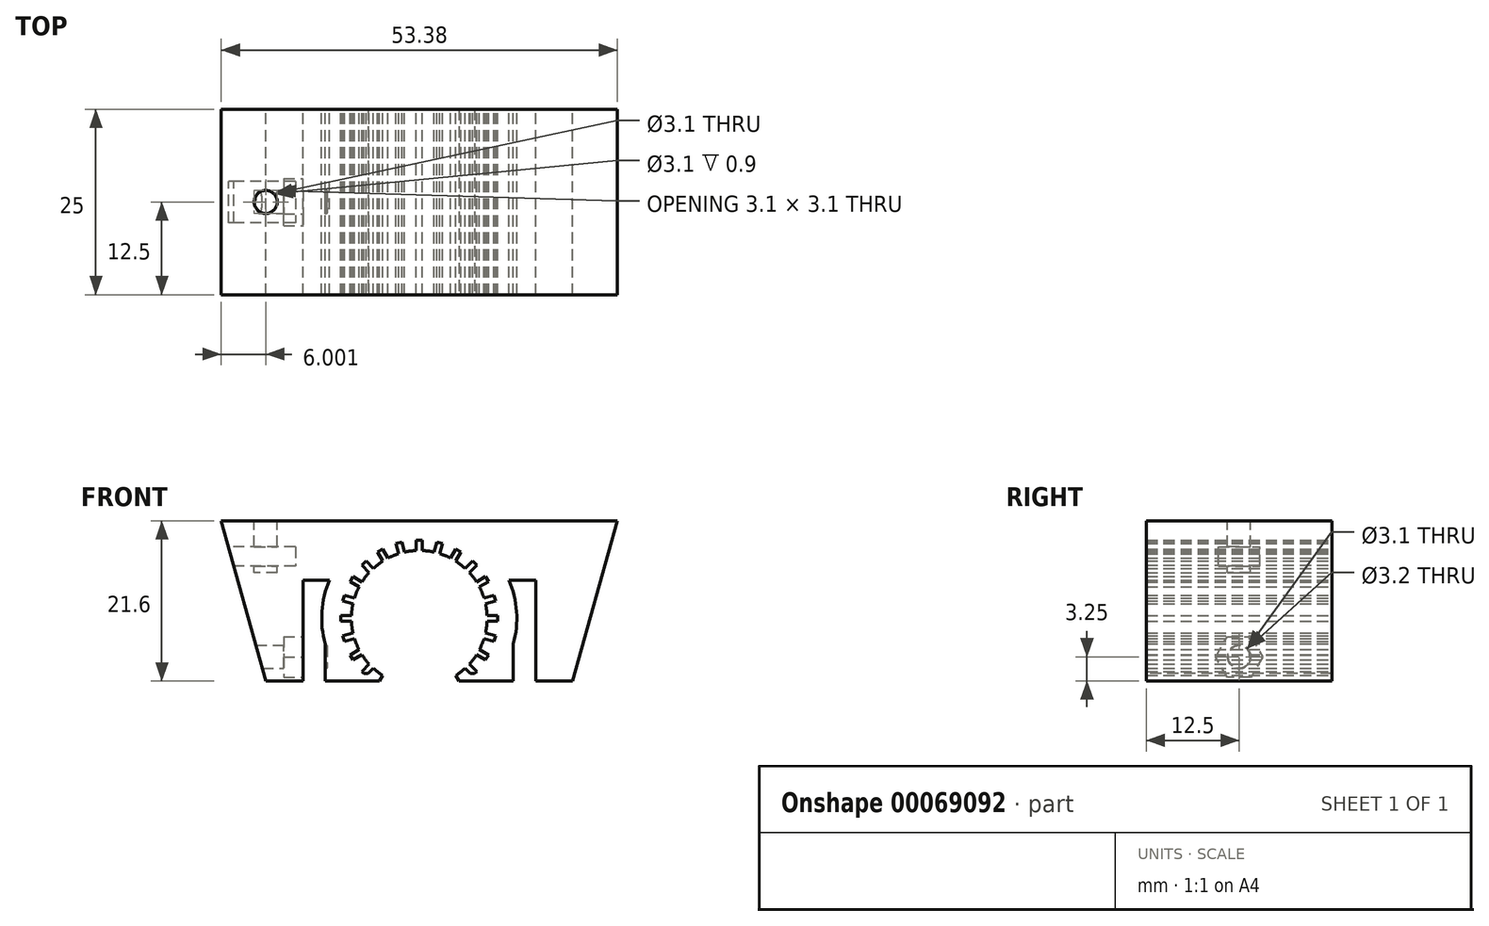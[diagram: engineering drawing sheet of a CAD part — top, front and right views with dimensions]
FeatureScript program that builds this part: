
annotation { "Feature Type Name" : "Feature", "Feature Type Description" : "" }
export const myFeature = defineFeature(function(context is Context, id is Id, definition is map)
    precondition{}
    {
        {
            var Q0;
            Q0=qCreatedBy(makeId("Front.planeOp"),FACE);
            var sketch = newSketch(context, id + "F0", { "sketchPlane" : qUnion([Q0])});
            skCircle(sketch, "E0", {"center": v(0, 0) * mm, "radius": 8.95 * mm, "construction": true});
            skLineSegment(sketch, "E1", {"start": v(-47.47, -8.95) * mm, "end": v(47.47, -8.95) * mm, "construction": true});
            skPoint(sketch, "E2", {"position": v(0, -8.95) * mm});
            skLineSegment(sketch, "E3", {"start": v(0, 13.15) * mm, "end": v(26.69, 13.15) * mm});
            skLineSegment(sketch, "E4", {"start": v(26.69, 13.15) * mm, "end": v(20.69, -8.45) * mm});
            skLineSegment(sketch, "E5", {"start": v(20.69, -8.45) * mm, "end": v(15.69, -8.45) * mm});
            skLineSegment(sketch, "E6", {"start": v(15.69, -8.45) * mm, "end": v(15.69, 5.15) * mm});
            skLineSegment(sketch, "E7", {"start": v(15.69, 5.15) * mm, "end": v(12.1, 5.15) * mm});
            skArc(sketch, "E8", {"start": v(3.5, -8.45) * mm, "mid": v(8.97, 1.79) * mm, "end": v(0, 9.15) * mm});
            skLineSegment(sketch, "E9", {"start": v(3.5, -8.45) * mm, "end": v(12.69, -8.45) * mm});
            skArc(sketch, "E10", {"start": v(12.69, -3.45) * mm, "mid": v(13.12, 0.9) * mm, "end": v(12.1, 5.15) * mm});
            skLineSegment(sketch, "E11", {"start": v(12.69, -3.45) * mm, "end": v(12.69, -8.45) * mm});
            skLineSegment(sketch, "E12", {"start": v(0, 0) * mm, "end": v(0, -8.95) * mm, "construction": true});
            skArc(sketch, "E13.MirrorCS", {"start": v(-12.69, -3.45) * mm, "mid": v(-13.12, 0.9) * mm, "end": v(-12.1, 5.15) * mm});
            skLineSegment(sketch, "E14.MirrorCS", {"start": v(0, 13.15) * mm, "end": v(-26.69, 13.15) * mm});
            skLineSegment(sketch, "E15.MirrorCS", {"start": v(-12.69, -3.45) * mm, "end": v(-12.69, -8.45) * mm});
            skLineSegment(sketch, "E16.MirrorCS", {"start": v(-3.5, -8.45) * mm, "end": v(-12.69, -8.45) * mm});
            skLineSegment(sketch, "E17.MirrorCS", {"start": v(-26.69, 13.15) * mm, "end": v(-20.69, -8.45) * mm});
            skLineSegment(sketch, "E18.MirrorCS", {"start": v(-15.69, -8.45) * mm, "end": v(-15.69, 5.15) * mm});
            skArc(sketch, "E19.MirrorCS", {"start": v(-3.5, -8.45) * mm, "mid": v(-8.97, 1.79) * mm, "end": v(0, 9.15) * mm});
            skLineSegment(sketch, "E20.MirrorCS", {"start": v(-15.69, 5.15) * mm, "end": v(-12.1, 5.15) * mm});
            skLineSegment(sketch, "E21.MirrorCS", {"start": v(-20.69, -8.45) * mm, "end": v(-15.69, -8.45) * mm});
            skSolve(sketch);
        }
        {
            var Q0;
            Q0=makeQuery(id+"F0.imprint","IMPRINT",FACE,{"disambiguationData":[TD([[makeQuery(id+"F0.imprint","IMPRINT",EDGE,{"derivedFrom":sQuery(id+"F0.wireOp",EDGE,"E3")}),-1.0]])]});
            extrude(context, id + "F1", {"entities" : qUnion([Q0]), "depth" : 25 * mm, "offsetDistance" : 25 * mm});
        }
        {
            var Q0;
            Q0=makeQuery(id+"F1.opExtrude","CAP_FACE",FACE,{"disambiguationData":[OSD([sQuery(id+"F0.wireOp",EDGE,"E3"),sQuery(id+"F0.wireOp",EDGE,"E4"),sQuery(id+"F0.wireOp",EDGE,"E5"),sQuery(id+"F0.wireOp",EDGE,"E6"),sQuery(id+"F0.wireOp",EDGE,"E7"),sQuery(id+"F0.wireOp",EDGE,"E8"),sQuery(id+"F0.wireOp",EDGE,"E9"),sQuery(id+"F0.wireOp",EDGE,"E10"),sQuery(id+"F0.wireOp",EDGE,"E11"),sQuery(id+"F0.wireOp",EDGE,"E13.MirrorCS"),sQuery(id+"F0.wireOp",EDGE,"E14.MirrorCS"),sQuery(id+"F0.wireOp",EDGE,"E15.MirrorCS"),sQuery(id+"F0.wireOp",EDGE,"E16.MirrorCS"),sQuery(id+"F0.wireOp",EDGE,"E17.MirrorCS"),sQuery(id+"F0.wireOp",EDGE,"E18.MirrorCS"),sQuery(id+"F0.wireOp",EDGE,"E19.MirrorCS"),sQuery(id+"F0.wireOp",EDGE,"E20.MirrorCS"),sQuery(id+"F0.wireOp",EDGE,"E21.MirrorCS")])],"isStart":true});
            var sketch = newSketch(context, id + "F2", { "sketchPlane" : qUnion([Q0])});
            skLineSegment(sketch, "E22.bottom", {"start": v(-10.55, 0.4) * mm, "end": v(-7.35, 0.4) * mm});
            skLineSegment(sketch, "E22.top", {"start": v(-10.55, -0.4) * mm, "end": v(-7.35, -0.4) * mm});
            skLineSegment(sketch, "E22.left", {"start": v(-10.55, 0.4) * mm, "end": v(-10.55, -0.4) * mm});
            skLineSegment(sketch, "E22.right", {"start": v(-7.35, 0.4) * mm, "end": v(-7.35, -0.4) * mm});
            skPoint(sketch, "E22.middle", {"position": v(-8.95, 0) * mm});
            skPoint(sketch, "E23.1.0", {"position": v(-8.65, -2.32) * mm});
            skLineSegment(sketch, "E23.1.1", {"start": v(-10.3, -2.34) * mm, "end": v(-7.2, -1.52) * mm});
            skLineSegment(sketch, "E23.1.2", {"start": v(-7.2, -1.52) * mm, "end": v(-7, -2.29) * mm});
            skLineSegment(sketch, "E23.1.3", {"start": v(-10.09, -3.12) * mm, "end": v(-7, -2.29) * mm});
            skLineSegment(sketch, "E23.1.4", {"start": v(-10.3, -2.34) * mm, "end": v(-10.09, -3.12) * mm});
            skPoint(sketch, "E23.2.0", {"position": v(-7.75, -4.47) * mm});
            skLineSegment(sketch, "E23.2.1", {"start": v(-9.34, -4.93) * mm, "end": v(-6.57, -3.33) * mm});
            skLineSegment(sketch, "E23.2.2", {"start": v(-6.57, -3.33) * mm, "end": v(-6.17, -4.02) * mm});
            skLineSegment(sketch, "E23.2.3", {"start": v(-8.94, -5.62) * mm, "end": v(-6.17, -4.02) * mm});
            skLineSegment(sketch, "E23.2.4", {"start": v(-9.34, -4.93) * mm, "end": v(-8.94, -5.62) * mm});
            skPoint(sketch, "E23.3.0", {"position": v(-6.33, -6.33) * mm});
            skLineSegment(sketch, "E23.3.1", {"start": v(-7.74, -7.18) * mm, "end": v(-5.48, -4.91) * mm});
            skLineSegment(sketch, "E23.3.2", {"start": v(-5.48, -4.91) * mm, "end": v(-4.91, -5.48) * mm});
            skLineSegment(sketch, "E23.3.3", {"start": v(-7.18, -7.74) * mm, "end": v(-4.91, -5.48) * mm});
            skLineSegment(sketch, "E23.3.4", {"start": v(-7.74, -7.18) * mm, "end": v(-7.18, -7.74) * mm});
            skPoint(sketch, "E23.4.0", {"position": v(-4.48, -7.75) * mm});
            skLineSegment(sketch, "E23.4.1", {"start": v(-5.62, -8.94) * mm, "end": v(-4.02, -6.17) * mm});
            skLineSegment(sketch, "E23.4.2", {"start": v(-4.02, -6.17) * mm, "end": v(-3.33, -6.57) * mm});
            skLineSegment(sketch, "E23.4.3", {"start": v(-4.93, -9.34) * mm, "end": v(-3.33, -6.57) * mm});
            skLineSegment(sketch, "E23.4.4", {"start": v(-5.62, -8.94) * mm, "end": v(-4.93, -9.34) * mm});
            skPoint(sketch, "E23.5.0", {"position": v(-2.32, -8.65) * mm});
            skLineSegment(sketch, "E23.5.1", {"start": v(-3.12, -10.09) * mm, "end": v(-2.29, -7) * mm});
            skLineSegment(sketch, "E23.5.2", {"start": v(-2.29, -7) * mm, "end": v(-1.52, -7.2) * mm});
            skLineSegment(sketch, "E23.5.3", {"start": v(-2.34, -10.3) * mm, "end": v(-1.52, -7.2) * mm});
            skLineSegment(sketch, "E23.5.4", {"start": v(-3.12, -10.09) * mm, "end": v(-2.34, -10.3) * mm});
            skPoint(sketch, "E23.6.0", {"position": v(0, -8.95) * mm});
            skLineSegment(sketch, "E23.6.1", {"start": v(-0.4, -10.55) * mm, "end": v(-0.4, -7.35) * mm});
            skLineSegment(sketch, "E23.6.2", {"start": v(-0.4, -7.35) * mm, "end": v(0.4, -7.35) * mm});
            skLineSegment(sketch, "E23.6.3", {"start": v(0.4, -10.55) * mm, "end": v(0.4, -7.35) * mm});
            skLineSegment(sketch, "E23.6.4", {"start": v(-0.4, -10.55) * mm, "end": v(0.4, -10.55) * mm});
            skPoint(sketch, "E23.7.0", {"position": v(2.32, -8.65) * mm});
            skLineSegment(sketch, "E23.7.1", {"start": v(2.34, -10.3) * mm, "end": v(1.52, -7.2) * mm});
            skLineSegment(sketch, "E23.7.2", {"start": v(1.52, -7.2) * mm, "end": v(2.29, -7) * mm});
            skLineSegment(sketch, "E23.7.3", {"start": v(3.12, -10.09) * mm, "end": v(2.29, -7) * mm});
            skLineSegment(sketch, "E23.7.4", {"start": v(2.34, -10.3) * mm, "end": v(3.12, -10.09) * mm});
            skPoint(sketch, "E23.8.0", {"position": v(4.47, -7.75) * mm});
            skLineSegment(sketch, "E23.8.1", {"start": v(4.93, -9.34) * mm, "end": v(3.33, -6.57) * mm});
            skLineSegment(sketch, "E23.8.2", {"start": v(3.33, -6.57) * mm, "end": v(4.02, -6.17) * mm});
            skLineSegment(sketch, "E23.8.3", {"start": v(5.62, -8.94) * mm, "end": v(4.02, -6.17) * mm});
            skLineSegment(sketch, "E23.8.4", {"start": v(4.93, -9.34) * mm, "end": v(5.62, -8.94) * mm});
            skPoint(sketch, "E23.9.0", {"position": v(6.33, -6.33) * mm});
            skLineSegment(sketch, "E23.9.1", {"start": v(7.18, -7.74) * mm, "end": v(4.91, -5.48) * mm});
            skLineSegment(sketch, "E23.9.2", {"start": v(4.91, -5.48) * mm, "end": v(5.48, -4.91) * mm});
            skLineSegment(sketch, "E23.9.3", {"start": v(7.74, -7.18) * mm, "end": v(5.48, -4.91) * mm});
            skLineSegment(sketch, "E23.9.4", {"start": v(7.18, -7.74) * mm, "end": v(7.74, -7.18) * mm});
            skPoint(sketch, "E23.10.0", {"position": v(7.75, -4.48) * mm});
            skLineSegment(sketch, "E23.10.1", {"start": v(8.94, -5.62) * mm, "end": v(6.17, -4.02) * mm});
            skLineSegment(sketch, "E23.10.2", {"start": v(6.17, -4.02) * mm, "end": v(6.57, -3.33) * mm});
            skLineSegment(sketch, "E23.10.3", {"start": v(9.34, -4.93) * mm, "end": v(6.57, -3.33) * mm});
            skLineSegment(sketch, "E23.10.4", {"start": v(8.94, -5.62) * mm, "end": v(9.34, -4.93) * mm});
            skPoint(sketch, "E23.11.0", {"position": v(8.65, -2.32) * mm});
            skLineSegment(sketch, "E23.11.1", {"start": v(10.09, -3.12) * mm, "end": v(7, -2.29) * mm});
            skLineSegment(sketch, "E23.11.2", {"start": v(7, -2.29) * mm, "end": v(7.2, -1.52) * mm});
            skLineSegment(sketch, "E23.11.3", {"start": v(10.3, -2.34) * mm, "end": v(7.2, -1.52) * mm});
            skLineSegment(sketch, "E23.11.4", {"start": v(10.09, -3.12) * mm, "end": v(10.3, -2.34) * mm});
            skPoint(sketch, "E23.12.0", {"position": v(8.95, 0) * mm});
            skLineSegment(sketch, "E23.12.1", {"start": v(10.55, -0.4) * mm, "end": v(7.35, -0.4) * mm});
            skLineSegment(sketch, "E23.12.2", {"start": v(7.35, -0.4) * mm, "end": v(7.35, 0.4) * mm});
            skLineSegment(sketch, "E23.12.3", {"start": v(10.55, 0.4) * mm, "end": v(7.35, 0.4) * mm});
            skLineSegment(sketch, "E23.12.4", {"start": v(10.55, -0.4) * mm, "end": v(10.55, 0.4) * mm});
            skPoint(sketch, "E23.13.0", {"position": v(8.65, 2.32) * mm});
            skLineSegment(sketch, "E23.13.1", {"start": v(10.3, 2.34) * mm, "end": v(7.2, 1.52) * mm});
            skLineSegment(sketch, "E23.13.2", {"start": v(7.2, 1.52) * mm, "end": v(7, 2.29) * mm});
            skLineSegment(sketch, "E23.13.3", {"start": v(10.09, 3.12) * mm, "end": v(7, 2.29) * mm});
            skLineSegment(sketch, "E23.13.4", {"start": v(10.3, 2.34) * mm, "end": v(10.09, 3.12) * mm});
            skPoint(sketch, "E23.14.0", {"position": v(7.75, 4.47) * mm});
            skLineSegment(sketch, "E23.14.1", {"start": v(9.34, 4.93) * mm, "end": v(6.57, 3.33) * mm});
            skLineSegment(sketch, "E23.14.2", {"start": v(6.57, 3.33) * mm, "end": v(6.17, 4.02) * mm});
            skLineSegment(sketch, "E23.14.3", {"start": v(8.94, 5.62) * mm, "end": v(6.17, 4.02) * mm});
            skLineSegment(sketch, "E23.14.4", {"start": v(9.34, 4.93) * mm, "end": v(8.94, 5.62) * mm});
            skPoint(sketch, "E23.15.0", {"position": v(6.33, 6.33) * mm});
            skLineSegment(sketch, "E23.15.1", {"start": v(7.74, 7.18) * mm, "end": v(5.48, 4.91) * mm});
            skLineSegment(sketch, "E23.15.2", {"start": v(5.48, 4.91) * mm, "end": v(4.91, 5.48) * mm});
            skLineSegment(sketch, "E23.15.3", {"start": v(7.18, 7.74) * mm, "end": v(4.91, 5.48) * mm});
            skLineSegment(sketch, "E23.15.4", {"start": v(7.74, 7.18) * mm, "end": v(7.18, 7.74) * mm});
            skPoint(sketch, "E23.16.0", {"position": v(4.48, 7.75) * mm});
            skLineSegment(sketch, "E23.16.1", {"start": v(5.62, 8.94) * mm, "end": v(4.02, 6.17) * mm});
            skLineSegment(sketch, "E23.16.2", {"start": v(4.02, 6.17) * mm, "end": v(3.33, 6.57) * mm});
            skLineSegment(sketch, "E23.16.3", {"start": v(4.93, 9.34) * mm, "end": v(3.33, 6.57) * mm});
            skLineSegment(sketch, "E23.16.4", {"start": v(5.62, 8.94) * mm, "end": v(4.93, 9.34) * mm});
            skPoint(sketch, "E23.17.0", {"position": v(2.32, 8.65) * mm});
            skLineSegment(sketch, "E23.17.1", {"start": v(3.12, 10.09) * mm, "end": v(2.29, 7) * mm});
            skLineSegment(sketch, "E23.17.2", {"start": v(2.29, 7) * mm, "end": v(1.52, 7.2) * mm});
            skLineSegment(sketch, "E23.17.3", {"start": v(2.34, 10.3) * mm, "end": v(1.52, 7.2) * mm});
            skLineSegment(sketch, "E23.17.4", {"start": v(3.12, 10.09) * mm, "end": v(2.34, 10.3) * mm});
            skPoint(sketch, "E23.center", {"position": v(0, 0) * mm});
            skLineSegment(sketch, "E24.1.18.0", {"start": v(0.4, 10.55) * mm, "end": v(0.4, 7.35) * mm});
            skLineSegment(sketch, "E24.4.18.0", {"start": v(0.4, 7.35) * mm, "end": v(-0.4, 7.35) * mm});
            skLineSegment(sketch, "E24.7.18.0", {"start": v(-0.4, 10.55) * mm, "end": v(-0.4, 7.35) * mm});
            skPoint(sketch, "E24.8.18.0", {"position": v(0, 8.95) * mm});
            skLineSegment(sketch, "E24.10.18.0", {"start": v(0.4, 10.55) * mm, "end": v(-0.4, 10.55) * mm});
            skLineSegment(sketch, "E24.1.19.0", {"start": v(-2.34, 10.3) * mm, "end": v(-1.52, 7.2) * mm});
            skLineSegment(sketch, "E24.4.19.0", {"start": v(-1.52, 7.2) * mm, "end": v(-2.29, 7) * mm});
            skLineSegment(sketch, "E24.7.19.0", {"start": v(-3.12, 10.09) * mm, "end": v(-2.29, 7) * mm});
            skPoint(sketch, "E24.8.19.0", {"position": v(-2.32, 8.65) * mm});
            skLineSegment(sketch, "E24.10.19.0", {"start": v(-2.34, 10.3) * mm, "end": v(-3.12, 10.09) * mm});
            skLineSegment(sketch, "E24.1.20.0", {"start": v(-4.93, 9.34) * mm, "end": v(-3.33, 6.57) * mm});
            skLineSegment(sketch, "E24.4.20.0", {"start": v(-3.33, 6.57) * mm, "end": v(-4.02, 6.17) * mm});
            skLineSegment(sketch, "E24.7.20.0", {"start": v(-5.62, 8.94) * mm, "end": v(-4.02, 6.17) * mm});
            skPoint(sketch, "E24.8.20.0", {"position": v(-4.47, 7.75) * mm});
            skLineSegment(sketch, "E24.10.20.0", {"start": v(-4.93, 9.34) * mm, "end": v(-5.62, 8.94) * mm});
            skLineSegment(sketch, "E24.1.21.0", {"start": v(-7.18, 7.74) * mm, "end": v(-4.91, 5.48) * mm});
            skLineSegment(sketch, "E24.4.21.0", {"start": v(-4.91, 5.48) * mm, "end": v(-5.48, 4.91) * mm});
            skLineSegment(sketch, "E24.7.21.0", {"start": v(-7.74, 7.18) * mm, "end": v(-5.48, 4.91) * mm});
            skPoint(sketch, "E24.8.21.0", {"position": v(-6.33, 6.33) * mm});
            skLineSegment(sketch, "E24.10.21.0", {"start": v(-7.18, 7.74) * mm, "end": v(-7.74, 7.18) * mm});
            skLineSegment(sketch, "E25.1.22.0", {"start": v(-8.94, 5.62) * mm, "end": v(-6.17, 4.02) * mm});
            skLineSegment(sketch, "E25.4.22.0", {"start": v(-6.17, 4.02) * mm, "end": v(-6.57, 3.33) * mm});
            skLineSegment(sketch, "E25.7.22.0", {"start": v(-9.34, 4.93) * mm, "end": v(-6.57, 3.33) * mm});
            skPoint(sketch, "E25.8.22.0", {"position": v(-7.75, 4.48) * mm});
            skLineSegment(sketch, "E25.10.22.0", {"start": v(-8.94, 5.62) * mm, "end": v(-9.34, 4.93) * mm});
            skLineSegment(sketch, "E25.1.23.0", {"start": v(-10.09, 3.12) * mm, "end": v(-7, 2.29) * mm});
            skLineSegment(sketch, "E25.4.23.0", {"start": v(-7, 2.29) * mm, "end": v(-7.2, 1.52) * mm});
            skLineSegment(sketch, "E25.7.23.0", {"start": v(-10.3, 2.34) * mm, "end": v(-7.2, 1.52) * mm});
            skPoint(sketch, "E25.8.23.0", {"position": v(-8.65, 2.32) * mm});
            skLineSegment(sketch, "E25.10.23.0", {"start": v(-10.09, 3.12) * mm, "end": v(-10.3, 2.34) * mm});
            skCircle(sketch, "E26.0", {"center": v(0, 0) * mm, "radius": 8.95 * mm, "construction": true});
            skLineSegment(sketch, "E27", {"start": v(-3.33, -6.57) * mm, "end": v(-2.29, -7) * mm});
            skLineSegment(sketch, "E28", {"start": v(-4.93, -9.34) * mm, "end": v(-3.12, -10.09) * mm});
            skLineSegment(sketch, "E29", {"start": v(3.33, -6.57) * mm, "end": v(2.29, -7) * mm});
            skLineSegment(sketch, "E30", {"start": v(4.93, -9.34) * mm, "end": v(3.12, -10.09) * mm});
            skSolve(sketch);
        }
        {
            var Q0;
            Q0 = qSketchRegion(id + "F2", true);
            extrude(context, id + "F3", {"entities" : qUnion([Q0]), "operationType" : NewBodyOperationType.REMOVE, "endBound" : BoundingType.THROUGH_ALL, "oppositeDirection" : true, "depth" : 25 * mm, "offsetDistance" : 25 * mm});
        }
        {
            var Q0;
            Q0=makeQuery(id+"F3.boolean.opBoolean","COPY",EDGE,{"derivedFrom":makeQuery(id+"F3.opExtrude","SWEPT_EDGE",EDGE,{"disambiguationData":[OSD([sQuery(id+"F2.wireOp",EDGE,"E23.3.3"),sQuery(id+"F2.wireOp",EDGE,"E23.3.4")])]})});
            var Q1;
            Q1=makeQuery(id+"F3.boolean.opBoolean","COPY",EDGE,{"derivedFrom":makeQuery(id+"F3.opExtrude","SWEPT_EDGE",EDGE,{"disambiguationData":[OSD([sQuery(id+"F2.wireOp",EDGE,"E23.9.1"),sQuery(id+"F2.wireOp",EDGE,"E23.9.4")])]})});
            chamfer(context, id + "F4", {"entities" : qUnion([Q0, Q1]), "width" : .4 * mm, "tangentPropagation" : true});
        }
        {
            var Q0;
            Q0=makeQuery(id+"F1.opExtrude","SWEPT_FACE",FACE,{"disambiguationData":[OSD([sQuery(id+"F0.wireOp",EDGE,"E18.MirrorCS")])]});
            var sketch = newSketch(context, id + "F5", { "sketchPlane" : qUnion([Q0])});
            skCircle(sketch, "E31", {"center": v(-12.5, -5.2) * mm, "radius": 1.55 * mm});
            skPoint(sketch, "E31.centerSnap0", {"position": v(-12.5, -8.45) * mm});
            skCircle(sketch, "E32.cCircle", {"center": v(-12.5, -5.2) * mm, "radius": 2.75 * mm, "construction": true});
            skLineSegment(sketch, "E32.0", {"start": v(-10.91, -7.95) * mm, "end": v(-14.09, -7.95) * mm});
            skLineSegment(sketch, "E32.1", {"start": v(-14.09, -7.95) * mm, "end": v(-15.68, -5.2) * mm});
            skLineSegment(sketch, "E32.2", {"start": v(-15.68, -5.2) * mm, "end": v(-14.09, -2.45) * mm});
            skLineSegment(sketch, "E32.3", {"start": v(-14.09, -2.45) * mm, "end": v(-10.91, -2.45) * mm});
            skLineSegment(sketch, "E32.4", {"start": v(-10.91, -2.45) * mm, "end": v(-9.32, -5.2) * mm});
            skLineSegment(sketch, "E32.5", {"start": v(-9.32, -5.2) * mm, "end": v(-10.91, -7.95) * mm});
            skPoint(sketch, "E32.0.midPoint", {"position": v(-12.5, -7.95) * mm});
            skSolve(sketch);
        }
        {
            var Q0;
            Q0=makeQuery(id+"F5.imprint","IMPRINT",FACE,{"disambiguationData":[TD([[makeQuery(id+"F5.imprint","IMPRINT",EDGE,{"derivedFrom":sQuery(id+"F5.wireOp",EDGE,"E31")}),1.0]])]});
            extrude(context, id + "F6", {"entities" : qUnion([Q0]), "operationType" : NewBodyOperationType.REMOVE, "endBound" : BoundingType.THROUGH_ALL, "oppositeDirection" : true, "depth" : 25 * mm, "offsetDistance" : 25 * mm});
        }
        {
            var Q0;
            Q0=makeQuery(id+"F5.imprint","IMPRINT",FACE,{"disambiguationData":[TD([[makeQuery(id+"F5.imprint","IMPRINT",EDGE,{"derivedFrom":sQuery(id+"F5.wireOp",EDGE,"E31")}),-1.0]])]});
            extrude(context, id + "F7", {"entities" : qUnion([Q0]), "operationType" : NewBodyOperationType.REMOVE, "oppositeDirection" : true, "depth" : 2.6 * mm, "offsetDistance" : 25 * mm});
        }
        {
            var Q0;
            Q0=makeQuery(id+"F1.opExtrude","SWEPT_FACE",FACE,{"disambiguationData":[OSD([sQuery(id+"F0.wireOp",EDGE,"E15.MirrorCS")])]});
            var sketch = newSketch(context, id + "F8", { "sketchPlane" : qUnion([Q0])});
            skPoint(sketch, "E33.0", {"position": v(12.5, -5.2) * mm});
            skCircle(sketch, "E34", {"center": v(12.5, -5.2) * mm, "radius": 1.6 * mm});
            skSolve(sketch);
        }
        {
            var Q0;
            Q0=makeQuery(id+"F8.imprint","IMPRINT",FACE,{"disambiguationData":[TD([[makeQuery(id+"F8.imprint","IMPRINT",EDGE,{"derivedFrom":sQuery(id+"F8.wireOp",EDGE,"E34")}),1.0]])]});
            extrude(context, id + "F9", {"entities" : qUnion([Q0]), "operationType" : NewBodyOperationType.REMOVE, "oppositeDirection" : true, "depth" : .3 * mm, "offsetDistance" : 25 * mm});
        }
        {
            var Q0;
            Q0=makeQuery(id+"F9.boolean.opBoolean","COPY",EDGE,{"derivedFrom":makeQuery(id+"F9.opExtrude","CAP_EDGE",EDGE,{"disambiguationData":[OSD([sQuery(id+"F8.wireOp",EDGE,"E34")])],"isStart":true})});
            var Q1;
            Q1=makeQuery(id+"F9.boolean.opBoolean","COPY",EDGE,{"derivedFrom":makeQuery(id+"F9.opExtrude","CAP_EDGE",EDGE,{"disambiguationData":[OSD([sQuery(id+"F8.wireOp",EDGE,"E34")])],"isStart":false})});
            chamfer(context, id + "F10", {"entities" : qUnion([Q0, Q1]), "width" : .1 * mm, "tangentPropagation" : true});
        }
        {
            var Q0;
            Q0=makeQuery(id+"F1.opExtrude","SWEPT_FACE",FACE,{"disambiguationData":[OSD([sQuery(id+"F0.wireOp",EDGE,"E3"),sQuery(id+"F0.wireOp",EDGE,"E14.MirrorCS")])]});
            var sketch = newSketch(context, id + "F11", { "sketchPlane" : qUnion([Q0])});
            skCircle(sketch, "E35", {"center": v(-20.69, -12.5) * mm, "radius": 1.55 * mm});
            skPoint(sketch, "E35.centerSnap0", {"position": v(-26.69, -12.5) * mm});
            skSolve(sketch);
        }
        {
            var Q0;
            Q0 = qSketchRegion(id + "F11", true);
            extrude(context, id + "F12", {"entities" : qUnion([Q0]), "operationType" : NewBodyOperationType.REMOVE, "oppositeDirection" : true, "depth" : 7 * mm, "offsetDistance" : 25 * mm});
        }
        {
            var Q0;
            Q0=makeQuery(id+"F1.opExtrude","SWEPT_EDGE",EDGE,{"disambiguationData":[OSD([sQuery(id+"F0.wireOp",EDGE,"E14.MirrorCS"),sQuery(id+"F0.wireOp",EDGE,"E17.MirrorCS")])]});
            cPoint(context, id + "F13", {"entities" : qUnion([Q0]), "parameter" : 0.5});
        }
        {
            var Q0;
            Q0=qCreatedBy(makeId("Right.planeOp"),FACE);
            var Q1;
            Q1 = qCreatedBy(id + "F13" ,VERTEX);
            cPlane(context, id + "F14", {"entities" : qUnion([Q0, Q1]), "cplaneType" : CPlaneType.PLANE_POINT, "offset" : 25 * mm, "width" : 150 * mm, "height" : 150 * mm});
        }
        {
            var Q0;
            Q0=qCreatedBy(id+"F14.planeOp",FACE);
            var sketch = newSketch(context, id + "F15", { "sketchPlane" : qUnion([Q0])});
            skPoint(sketch, "E36.0", {"position": v(-12.5, 13.15) * mm});
            skLineSegment(sketch, "E37.bottom", {"start": v(-9.7, 9.65) * mm, "end": v(-15.3, 9.65) * mm});
            skLineSegment(sketch, "E37.top", {"start": v(-9.7, 7.05) * mm, "end": v(-15.3, 7.05) * mm});
            skLineSegment(sketch, "E37.left", {"start": v(-9.7, 9.65) * mm, "end": v(-9.7, 7.05) * mm});
            skLineSegment(sketch, "E37.right", {"start": v(-15.3, 9.65) * mm, "end": v(-15.3, 7.05) * mm});
            skPoint(sketch, "E37.middle", {"position": v(-12.5, 8.35) * mm});
            skSolve(sketch);
        }
        {
            var Q0;
            Q0 = qSketchRegion(id + "F15", true);
            extrude(context, id + "F16", {"entities" : qUnion([Q0]), "operationType" : NewBodyOperationType.REMOVE, "depth" : 10 * mm, "offsetDistance" : 25 * mm});
        }
    });
